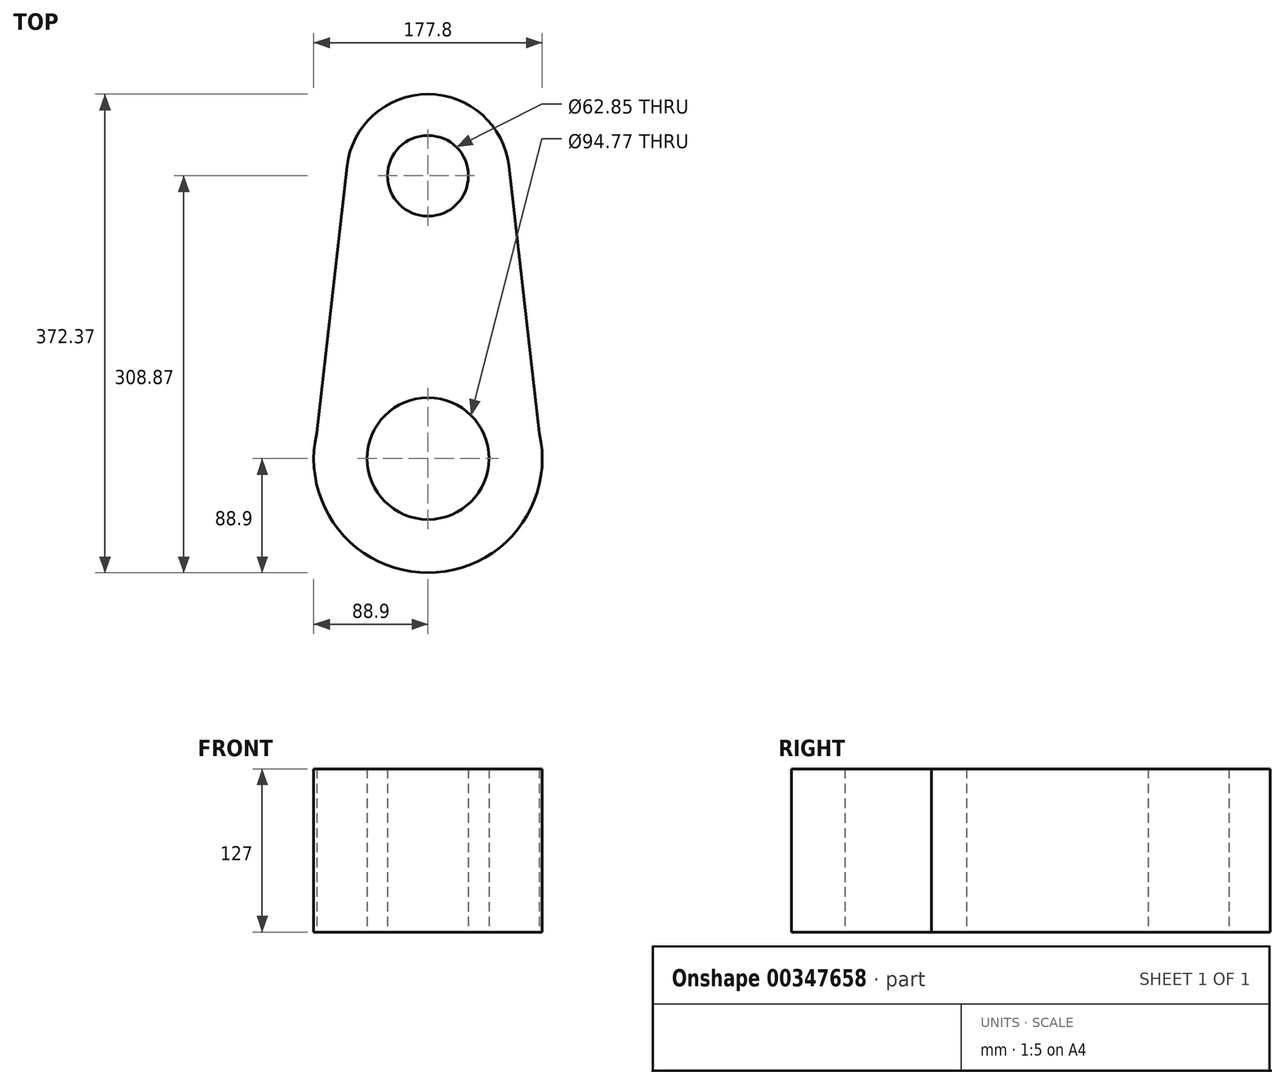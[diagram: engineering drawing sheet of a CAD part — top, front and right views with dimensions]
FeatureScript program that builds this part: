
annotation { "Feature Type Name" : "Feature", "Feature Type Description" : "" }
export const myFeature = defineFeature(function(context is Context, id is Id, definition is map)
    precondition{}
    {
        {
            var Q0;
            Q0=qCreatedBy(makeId("Top.planeOp"),FACE);
            var sketch = newSketch(context, id + "F0", { "sketchPlane" : qUnion([Q0])});
            skCircle(sketch, "E0", {"center": v(0, 0) * mm, "radius": 47.39 * mm});
            skCircle(sketch, "E1", {"center": v(0, 0) * mm, "radius": 88.9 * mm});
            skCircle(sketch, "E2", {"center": v(0, 219.97) * mm, "radius": 31.43 * mm});
            skCircle(sketch, "E3", {"center": v(0, 219.97) * mm, "radius": 63.5 * mm});
            skLineSegment(sketch, "E4", {"start": v(-88.9, 0) * mm, "end": v(-63.1, 227.14) * mm});
            skLineSegment(sketch, "E5", {"start": v(88.9, 0) * mm, "end": v(63.1, 227.14) * mm});
            skSolve(sketch);
        }
        {
            var Q0;
            Q0 = qSketchRegion(id + "F0", true);
            var Q1;
            Q1=makeQuery(id+"F0.imprint","IMPRINT",FACE,{"disambiguationData":[TD([[makeQuery(id+"F0.imprint","IMPRINT",EDGE,{"derivedFrom":sQuery(id+"F0.wireOp",EDGE,"E0")}),-1.0]])]});
            extrude(context, id + "F1", {"entities" : qUnion([Q0, Q1]), "depth" : 127 * mm});
        }
    });
